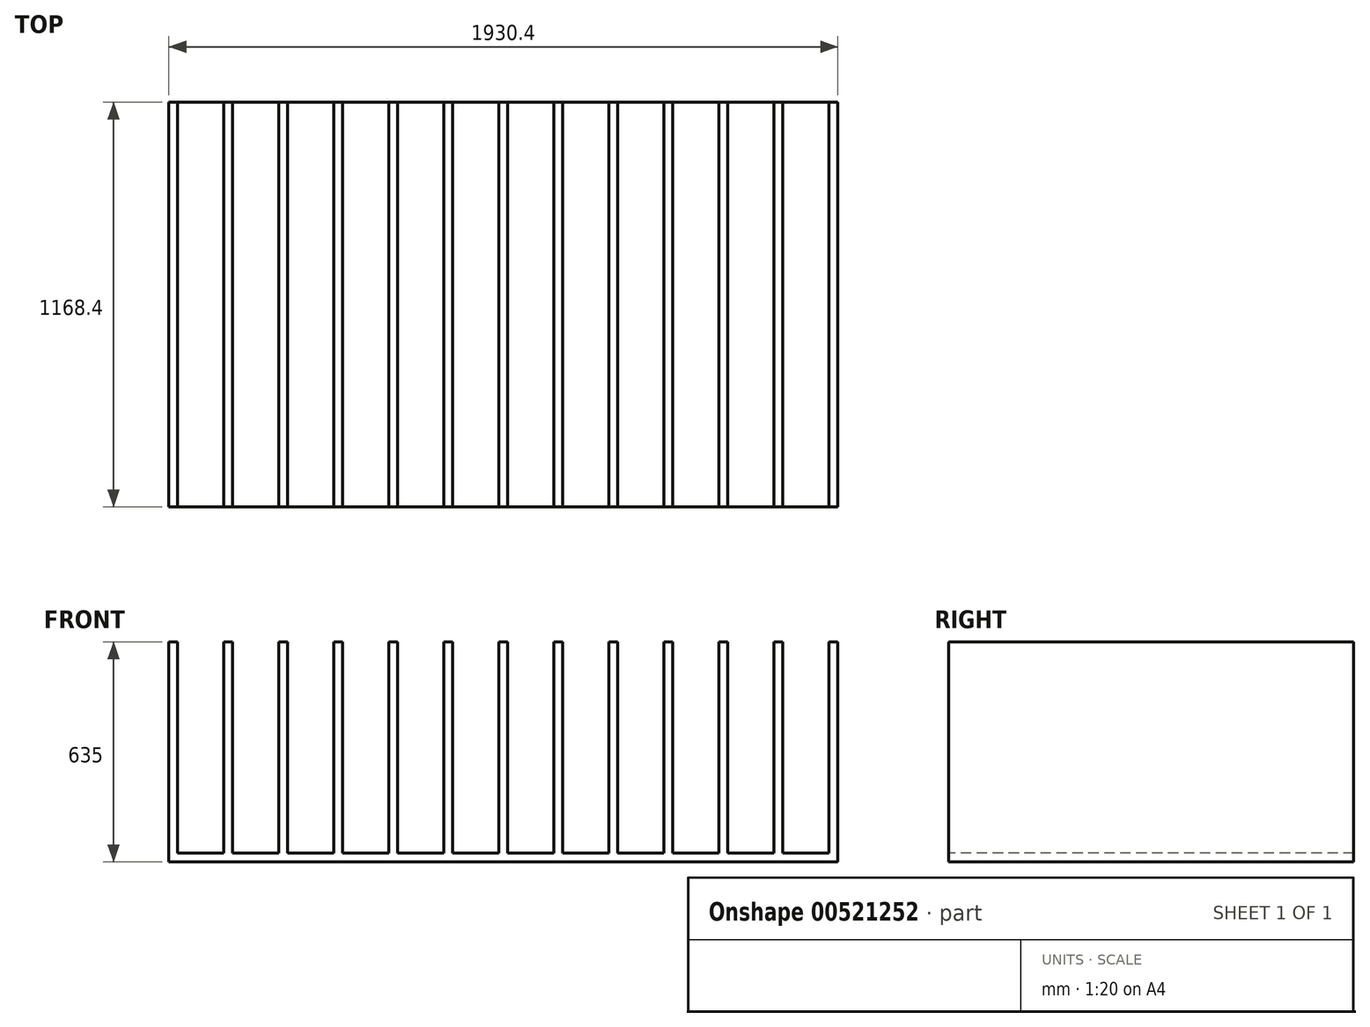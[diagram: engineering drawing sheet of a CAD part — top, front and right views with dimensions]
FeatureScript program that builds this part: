
annotation { "Feature Type Name" : "Feature", "Feature Type Description" : "" }
export const myFeature = defineFeature(function(context is Context, id is Id, definition is map)
    precondition{}
    {
        {
            var Q0;
            Q0=qCreatedBy(makeId("Top.planeOp"),FACE);
            var sketch = newSketch(context, id + "F0", { "sketchPlane" : qUnion([Q0])});
            skLineSegment(sketch, "E0.bottom", {"start": v(965.2, -584.2) * mm, "end": v(-965.2, -584.2) * mm});
            skLineSegment(sketch, "E0.top", {"start": v(965.2, 584.2) * mm, "end": v(-965.2, 584.2) * mm});
            skLineSegment(sketch, "E0.left", {"start": v(965.2, -584.2) * mm, "end": v(965.2, 584.2) * mm});
            skLineSegment(sketch, "E0.right", {"start": v(-965.2, -584.2) * mm, "end": v(-965.2, 584.2) * mm});
            skPoint(sketch, "E0.middle", {"position": v(0, 0) * mm});
            skSolve(sketch);
        }
        {
            var Q0;
            Q0 = qSketchRegion(id + "F0", true);
            extrude(context, id + "F1", {"entities" : qUnion([Q0]), "depth" : 25.4 * mm, "offsetDistance" : 25.4 * mm});
        }
        {
            var Q0;
            Q0=makeQuery(id+"F1.opExtrude","CAP_FACE",FACE,{"disambiguationData":[OSD([sQuery(id+"F0.wireOp",EDGE,"E0.bottom"),sQuery(id+"F0.wireOp",EDGE,"E0.top"),sQuery(id+"F0.wireOp",EDGE,"E0.left"),sQuery(id+"F0.wireOp",EDGE,"E0.right")])],"isStart":false});
            var sketch = newSketch(context, id + "F2", { "sketchPlane" : qUnion([Q0])});
            skLineSegment(sketch, "E1", {"start": v(-965.2, 584.2) * mm, "end": v(-939.8, 584.2) * mm, "construction": true});
            skLineSegment(sketch, "E2", {"start": v(-939.8, 584.2) * mm, "end": v(-806.45, 584.2) * mm, "construction": true});
            skLineSegment(sketch, "E3", {"start": v(-806.45, 584.2) * mm, "end": v(-781.05, 584.2) * mm, "construction": true});
            skLineSegment(sketch, "E4", {"start": v(-781.05, 584.2) * mm, "end": v(-647.7, 584.2) * mm, "construction": true});
            skLineSegment(sketch, "E5", {"start": v(-647.7, 584.2) * mm, "end": v(-622.3, 584.2) * mm, "construction": true});
            skLineSegment(sketch, "E6", {"start": v(-622.3, 584.2) * mm, "end": v(-488.95, 584.2) * mm, "construction": true});
            skLineSegment(sketch, "E7", {"start": v(-488.95, 584.2) * mm, "end": v(-463.55, 584.2) * mm, "construction": true});
            skLineSegment(sketch, "E8", {"start": v(-463.55, 584.2) * mm, "end": v(-330.2, 584.2) * mm, "construction": true});
            skLineSegment(sketch, "E9", {"start": v(-330.2, 584.2) * mm, "end": v(-304.8, 584.2) * mm, "construction": true});
            skLineSegment(sketch, "E10", {"start": v(-304.8, 584.2) * mm, "end": v(-171.45, 584.2) * mm, "construction": true});
            skLineSegment(sketch, "E11", {"start": v(-171.45, 584.2) * mm, "end": v(-146.05, 584.2) * mm, "construction": true});
            skLineSegment(sketch, "E12", {"start": v(-146.05, 584.2) * mm, "end": v(-12.7, 584.2) * mm, "construction": true});
            skLineSegment(sketch, "E13", {"start": v(-12.7, 584.2) * mm, "end": v(12.7, 584.2) * mm, "construction": true});
            skLineSegment(sketch, "E14", {"start": v(12.7, 584.2) * mm, "end": v(146.05, 584.2) * mm, "construction": true});
            skLineSegment(sketch, "E15", {"start": v(146.05, 584.2) * mm, "end": v(171.45, 584.2) * mm, "construction": true});
            skLineSegment(sketch, "E16", {"start": v(171.45, 584.2) * mm, "end": v(304.8, 584.2) * mm, "construction": true});
            skLineSegment(sketch, "E17", {"start": v(304.8, 584.2) * mm, "end": v(330.2, 584.2) * mm, "construction": true});
            skLineSegment(sketch, "E18", {"start": v(330.2, 584.2) * mm, "end": v(463.55, 584.2) * mm, "construction": true});
            skLineSegment(sketch, "E19", {"start": v(463.55, 584.2) * mm, "end": v(488.95, 584.2) * mm, "construction": true});
            skLineSegment(sketch, "E20", {"start": v(488.95, 584.2) * mm, "end": v(622.3, 584.2) * mm, "construction": true});
            skLineSegment(sketch, "E21", {"start": v(622.3, 584.2) * mm, "end": v(647.7, 584.2) * mm, "construction": true});
            skLineSegment(sketch, "E22", {"start": v(647.7, 584.2) * mm, "end": v(781.05, 584.2) * mm, "construction": true});
            skLineSegment(sketch, "E23", {"start": v(781.05, 584.2) * mm, "end": v(806.45, 584.2) * mm, "construction": true});
            skLineSegment(sketch, "E24", {"start": v(806.45, 584.2) * mm, "end": v(939.8, 584.2) * mm, "construction": true});
            skLineSegment(sketch, "E25", {"start": v(939.8, 584.2) * mm, "end": v(965.2, 584.2) * mm, "construction": true});
            skLineSegment(sketch, "E26.bottom", {"start": v(-939.8, 584.2) * mm, "end": v(-965.2, 584.2) * mm});
            skLineSegment(sketch, "E26.top", {"start": v(-939.8, -584.2) * mm, "end": v(-965.2, -584.2) * mm});
            skLineSegment(sketch, "E26.left", {"start": v(-939.8, 584.2) * mm, "end": v(-939.8, -584.2) * mm});
            skLineSegment(sketch, "E26.right", {"start": v(-965.2, 584.2) * mm, "end": v(-965.2, -584.2) * mm});
            skLineSegment(sketch, "E27.bottom", {"start": v(-781.05, 584.2) * mm, "end": v(-806.45, 584.2) * mm});
            skLineSegment(sketch, "E27.top", {"start": v(-781.05, -584.2) * mm, "end": v(-806.45, -584.2) * mm});
            skLineSegment(sketch, "E27.left", {"start": v(-781.05, 584.2) * mm, "end": v(-781.05, -584.2) * mm});
            skLineSegment(sketch, "E27.right", {"start": v(-806.45, 584.2) * mm, "end": v(-806.45, -584.2) * mm});
            skLineSegment(sketch, "E28.bottom", {"start": v(-622.3, 584.2) * mm, "end": v(-647.7, 584.2) * mm});
            skLineSegment(sketch, "E28.top", {"start": v(-622.3, -584.2) * mm, "end": v(-647.7, -584.2) * mm});
            skLineSegment(sketch, "E28.left", {"start": v(-622.3, 584.2) * mm, "end": v(-622.3, -584.2) * mm});
            skLineSegment(sketch, "E28.right", {"start": v(-647.7, 584.2) * mm, "end": v(-647.7, -584.2) * mm});
            skLineSegment(sketch, "E29.bottom", {"start": v(-463.55, 584.2) * mm, "end": v(-488.95, 584.2) * mm});
            skLineSegment(sketch, "E29.top", {"start": v(-463.55, -584.2) * mm, "end": v(-488.95, -584.2) * mm});
            skLineSegment(sketch, "E29.left", {"start": v(-463.55, 584.2) * mm, "end": v(-463.55, -584.2) * mm});
            skLineSegment(sketch, "E29.right", {"start": v(-488.95, 584.2) * mm, "end": v(-488.95, -584.2) * mm});
            skLineSegment(sketch, "E30.bottom", {"start": v(-304.8, 584.2) * mm, "end": v(-330.2, 584.2) * mm});
            skLineSegment(sketch, "E30.top", {"start": v(-304.8, -584.2) * mm, "end": v(-330.2, -584.2) * mm});
            skLineSegment(sketch, "E30.left", {"start": v(-304.8, 584.2) * mm, "end": v(-304.8, -584.2) * mm});
            skLineSegment(sketch, "E30.right", {"start": v(-330.2, 584.2) * mm, "end": v(-330.2, -584.2) * mm});
            skLineSegment(sketch, "E31.bottom", {"start": v(-146.05, 584.2) * mm, "end": v(-171.45, 584.2) * mm});
            skLineSegment(sketch, "E31.top", {"start": v(-146.05, -584.2) * mm, "end": v(-171.45, -584.2) * mm});
            skLineSegment(sketch, "E31.left", {"start": v(-146.05, 584.2) * mm, "end": v(-146.05, -584.2) * mm});
            skLineSegment(sketch, "E31.right", {"start": v(-171.45, 584.2) * mm, "end": v(-171.45, -584.2) * mm});
            skLineSegment(sketch, "E32.bottom", {"start": v(12.7, 584.2) * mm, "end": v(-12.7, 584.2) * mm});
            skLineSegment(sketch, "E32.top", {"start": v(12.7, -584.2) * mm, "end": v(-12.7, -584.2) * mm});
            skLineSegment(sketch, "E32.left", {"start": v(12.7, 584.2) * mm, "end": v(12.7, -584.2) * mm});
            skLineSegment(sketch, "E32.right", {"start": v(-12.7, 584.2) * mm, "end": v(-12.7, -584.2) * mm});
            skLineSegment(sketch, "E33.bottom", {"start": v(171.45, 584.2) * mm, "end": v(146.05, 584.2) * mm});
            skLineSegment(sketch, "E33.top", {"start": v(171.45, -584.2) * mm, "end": v(146.05, -584.2) * mm});
            skLineSegment(sketch, "E33.left", {"start": v(171.45, 584.2) * mm, "end": v(171.45, -584.2) * mm});
            skLineSegment(sketch, "E33.right", {"start": v(146.05, 584.2) * mm, "end": v(146.05, -584.2) * mm});
            skLineSegment(sketch, "E34.bottom", {"start": v(330.2, 584.2) * mm, "end": v(304.8, 584.2) * mm});
            skLineSegment(sketch, "E34.top", {"start": v(330.2, -584.2) * mm, "end": v(304.8, -584.2) * mm});
            skLineSegment(sketch, "E34.left", {"start": v(330.2, 584.2) * mm, "end": v(330.2, -584.2) * mm});
            skLineSegment(sketch, "E34.right", {"start": v(304.8, 584.2) * mm, "end": v(304.8, -584.2) * mm});
            skLineSegment(sketch, "E35.bottom", {"start": v(488.95, 584.2) * mm, "end": v(463.55, 584.2) * mm});
            skLineSegment(sketch, "E35.top", {"start": v(488.95, -584.2) * mm, "end": v(463.55, -584.2) * mm});
            skLineSegment(sketch, "E35.left", {"start": v(488.95, 584.2) * mm, "end": v(488.95, -584.2) * mm});
            skLineSegment(sketch, "E35.right", {"start": v(463.55, 584.2) * mm, "end": v(463.55, -584.2) * mm});
            skLineSegment(sketch, "E36.bottom", {"start": v(647.7, 584.2) * mm, "end": v(622.3, 584.2) * mm});
            skLineSegment(sketch, "E36.top", {"start": v(647.7, -584.2) * mm, "end": v(622.3, -584.2) * mm});
            skLineSegment(sketch, "E36.left", {"start": v(647.7, 584.2) * mm, "end": v(647.7, -584.2) * mm});
            skLineSegment(sketch, "E36.right", {"start": v(622.3, 584.2) * mm, "end": v(622.3, -584.2) * mm});
            skLineSegment(sketch, "E37.bottom", {"start": v(806.45, 584.2) * mm, "end": v(781.05, 584.2) * mm});
            skLineSegment(sketch, "E37.top", {"start": v(806.45, -584.2) * mm, "end": v(781.05, -584.2) * mm});
            skLineSegment(sketch, "E37.left", {"start": v(806.45, 584.2) * mm, "end": v(806.45, -584.2) * mm});
            skLineSegment(sketch, "E37.right", {"start": v(781.05, 584.2) * mm, "end": v(781.05, -584.2) * mm});
            skLineSegment(sketch, "E38.bottom", {"start": v(939.8, 584.2) * mm, "end": v(965.2, 584.2) * mm});
            skLineSegment(sketch, "E38.top", {"start": v(939.8, -584.2) * mm, "end": v(965.2, -584.2) * mm});
            skLineSegment(sketch, "E38.left", {"start": v(939.8, 584.2) * mm, "end": v(939.8, -584.2) * mm});
            skLineSegment(sketch, "E38.right", {"start": v(965.2, 584.2) * mm, "end": v(965.2, -584.2) * mm});
            skSolve(sketch);
        }
        {
            var Q0;
            Q0 = qSketchRegion(id + "F2", true);
            extrude(context, id + "F3", {"entities" : qUnion([Q0]), "operationType" : NewBodyOperationType.ADD, "depth" : 609.6 * mm, "offsetDistance" : 25.4 * mm});
        }
    });
